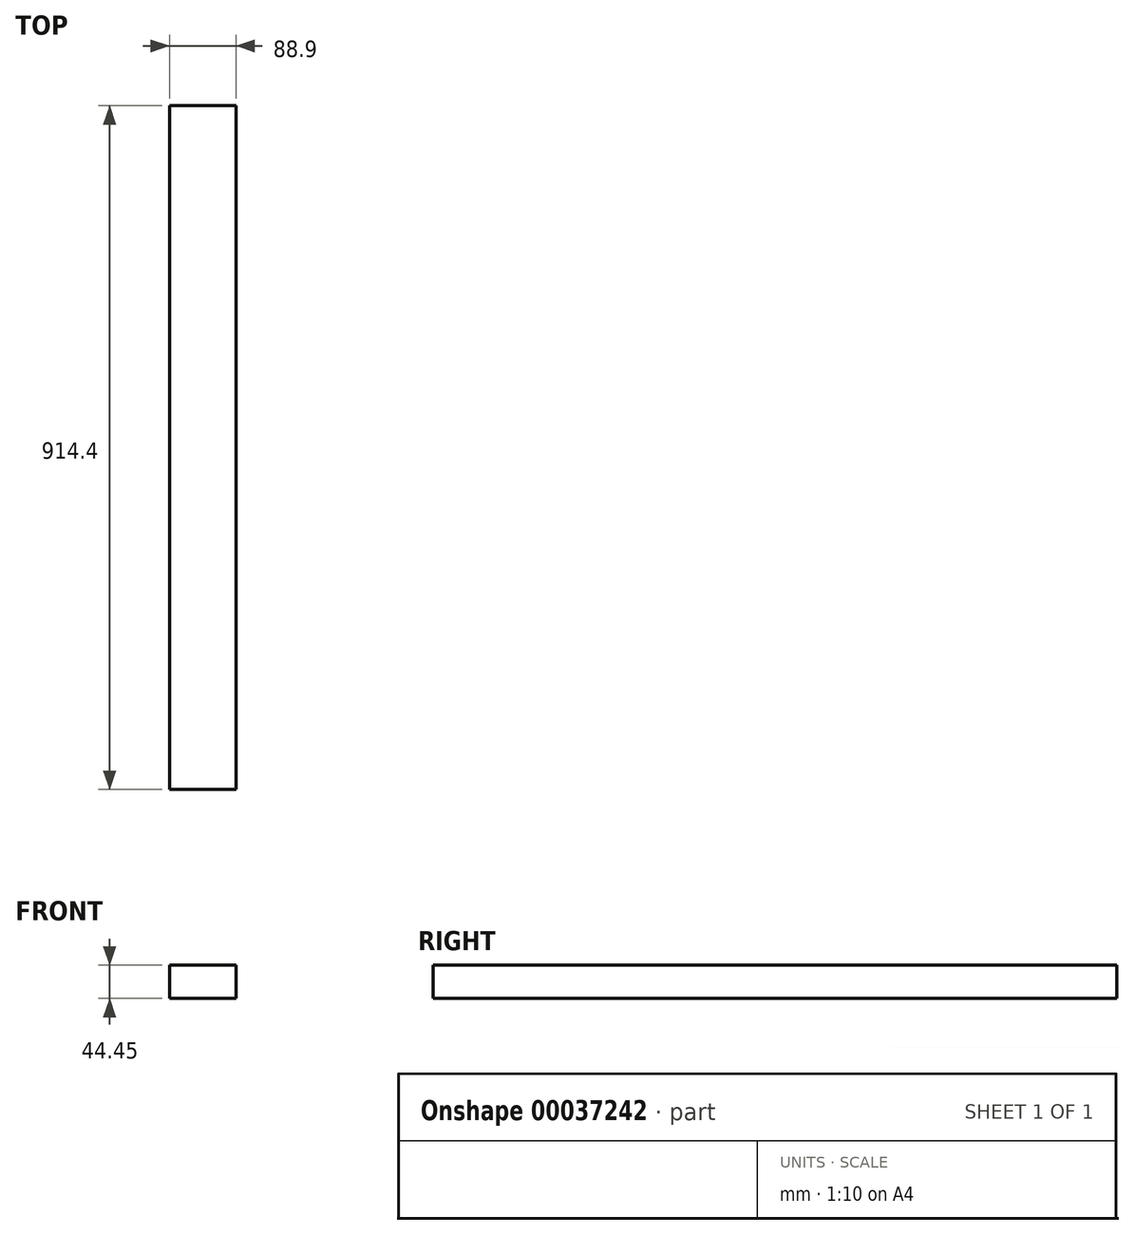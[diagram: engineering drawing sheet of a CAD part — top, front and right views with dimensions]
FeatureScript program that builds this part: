
annotation { "Feature Type Name" : "Feature", "Feature Type Description" : "" }
export const myFeature = defineFeature(function(context is Context, id is Id, definition is map)
    precondition{}
    {
        {
            var Q0;
            Q0=qCreatedBy(makeId("Front.planeOp"),FACE);
            var sketch = newSketch(context, id + "F0", { "sketchPlane" : qUnion([Q0])});
            skLineSegment(sketch, "E0.bottom", {"start": v(0, 0) * mm, "end": v(88.9, 0) * mm});
            skLineSegment(sketch, "E0.top", {"start": v(0, 44.45) * mm, "end": v(88.9, 44.45) * mm});
            skLineSegment(sketch, "E0.left", {"start": v(0, 0) * mm, "end": v(0, 44.45) * mm});
            skLineSegment(sketch, "E0.right", {"start": v(88.9, 0) * mm, "end": v(88.9, 44.45) * mm});
            skSolve(sketch);
        }
        {
            var Q0;
            Q0=makeQuery(id+"F0.imprint","IMPRINT",FACE,{"disambiguationData":[TD([[makeQuery(id+"F0.imprint","IMPRINT",EDGE,{"derivedFrom":sQuery(id+"F0.wireOp",EDGE,"E0.bottom")}),1.0]])]});
            extrude(context, id + "F1", {"entities" : qUnion([Q0]), "depth" : 914.4 * mm});
        }
    });
